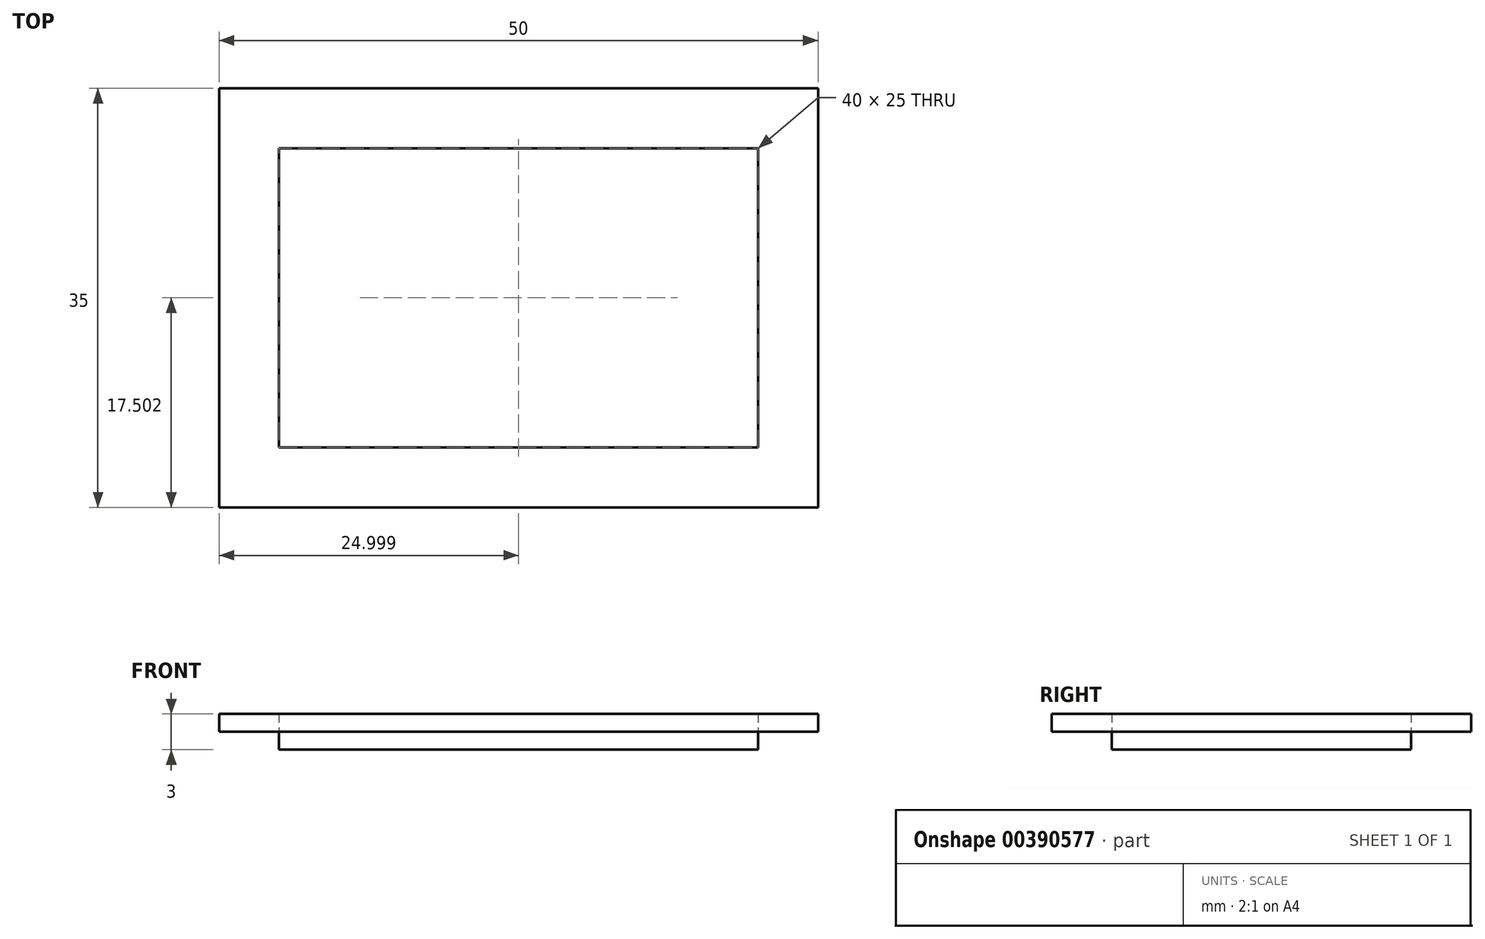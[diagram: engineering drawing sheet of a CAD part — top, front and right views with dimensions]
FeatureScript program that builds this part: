
annotation { "Feature Type Name" : "Feature", "Feature Type Description" : "" }
export const myFeature = defineFeature(function(context is Context, id is Id, definition is map)
    precondition{}
    {
        {
            var Q0;
            Q0=qCreatedBy(makeId("Top.planeOp"),FACE);
            var sketch = newSketch(context, id + "F0", { "sketchPlane" : qUnion([Q0])});
            skLineSegment(sketch, "E0.bottom", {"start": v(-57, 44.63) * mm, "end": v(-17, 44.63) * mm});
            skLineSegment(sketch, "E0.top", {"start": v(-57, 19.63) * mm, "end": v(-17, 19.63) * mm});
            skLineSegment(sketch, "E0.left", {"start": v(-57, 44.63) * mm, "end": v(-57, 19.63) * mm});
            skLineSegment(sketch, "E0.right", {"start": v(-17, 44.63) * mm, "end": v(-17, 19.63) * mm});
            skSolve(sketch);
        }
        {
            var Q0;
            Q0=makeQuery(id+"F0.imprint","IMPRINT",FACE,{"disambiguationData":[TD([[makeQuery(id+"F0.imprint","IMPRINT",EDGE,{"derivedFrom":sQuery(id+"F0.wireOp",EDGE,"E0.bottom")}),-1.0]])]});
            extrude(context, id + "F1", {"entities" : qUnion([Q0]), "depth" : 1.5 * mm});
        }
        {
            var Q0;
            Q0=makeQuery(id+"F1.opExtrude","CAP_FACE",FACE,{"disambiguationData":[OSD([sQuery(id+"F0.wireOp",EDGE,"E0.bottom"),sQuery(id+"F0.wireOp",EDGE,"E0.top"),sQuery(id+"F0.wireOp",EDGE,"E0.left"),sQuery(id+"F0.wireOp",EDGE,"E0.right")])],"isStart":false});
            var sketch = newSketch(context, id + "F2", { "sketchPlane" : qUnion([Q0])});
            skLineSegment(sketch, "E1.bottom", {"start": v(-57, 44.63) * mm, "end": v(-17, 44.63) * mm});
            skLineSegment(sketch, "E1.top", {"start": v(-57, 19.63) * mm, "end": v(-17, 19.63) * mm});
            skLineSegment(sketch, "E1.left", {"start": v(-57, 44.63) * mm, "end": v(-57, 19.63) * mm});
            skLineSegment(sketch, "E1.right", {"start": v(-17, 44.63) * mm, "end": v(-17, 19.63) * mm});
            skLineSegment(sketch, "E2.0", {"start": v(-55, 42.63) * mm, "end": v(-19, 42.63) * mm});
            skLineSegment(sketch, "E2.1", {"start": v(-55, 42.63) * mm, "end": v(-55, 21.63) * mm});
            skLineSegment(sketch, "E2.2", {"start": v(-55, 21.63) * mm, "end": v(-19, 21.63) * mm});
            skLineSegment(sketch, "E2.3", {"start": v(-19, 42.63) * mm, "end": v(-19, 21.63) * mm});
            skLineSegment(sketch, "E3.0", {"start": v(-62, 49.63) * mm, "end": v(-62, 14.63) * mm});
            skLineSegment(sketch, "E3.1", {"start": v(-12, 49.63) * mm, "end": v(-62, 49.63) * mm});
            skLineSegment(sketch, "E3.2", {"start": v(-12, 14.63) * mm, "end": v(-12, 49.63) * mm});
            skLineSegment(sketch, "E3.3", {"start": v(-62, 14.63) * mm, "end": v(-12, 14.63) * mm});
            skSolve(sketch);
        }
        {
            var Q0;
            Q0 = qSketchRegion(id + "F2", true);
            extrude(context, id + "F3", {"entities" : qUnion([Q0]), "depth" : 1.5 * mm});
        }
    });
